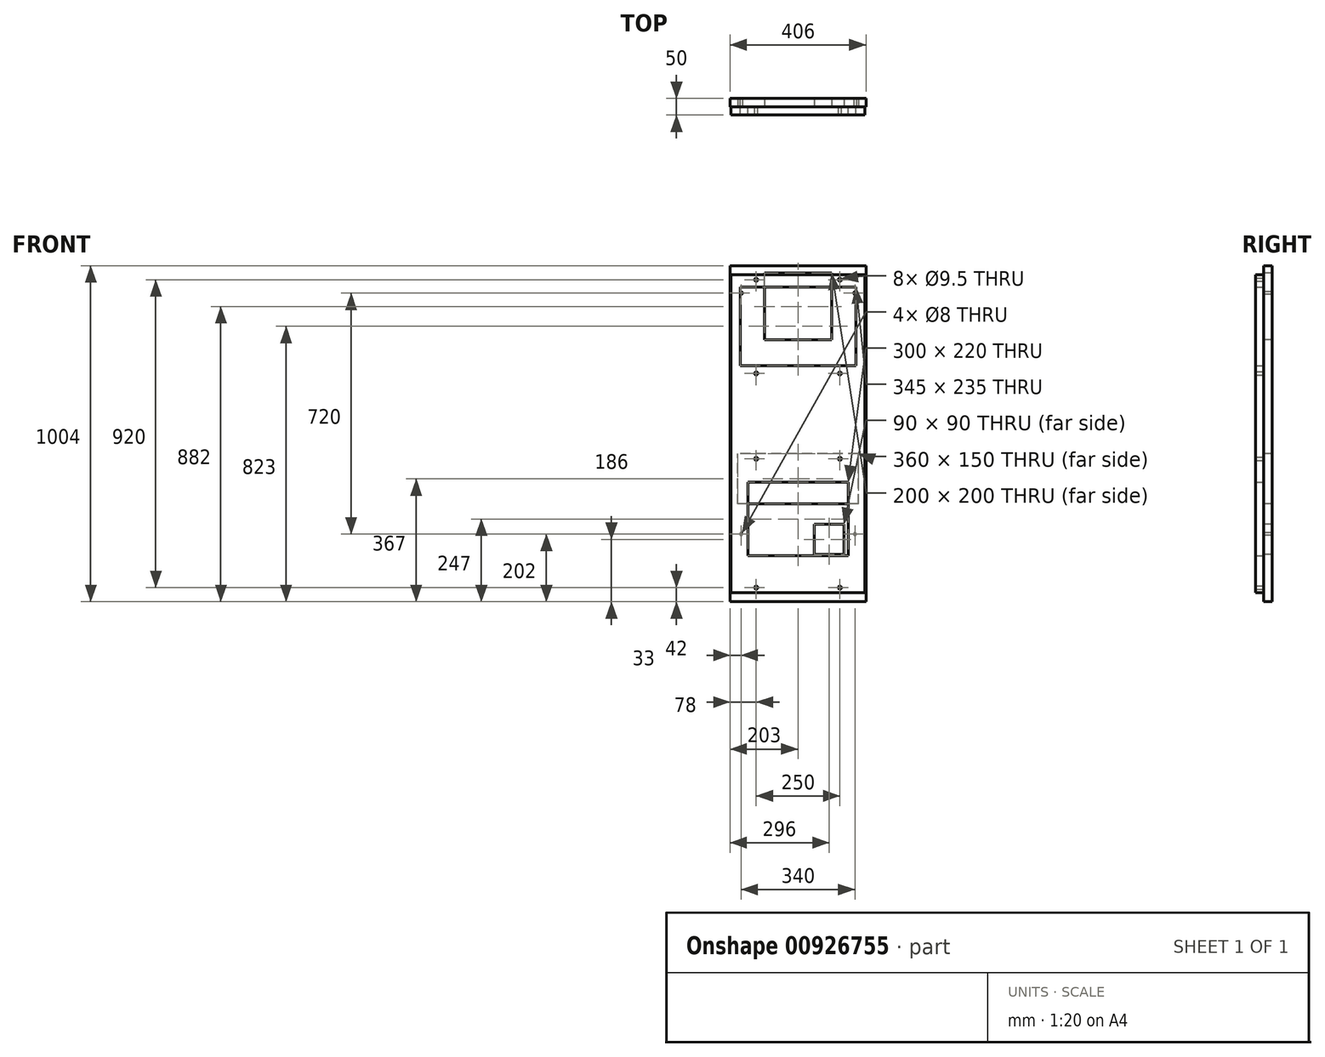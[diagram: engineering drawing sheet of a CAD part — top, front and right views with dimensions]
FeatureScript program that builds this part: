
annotation { "Feature Type Name" : "Feature", "Feature Type Description" : "" }
export const myFeature = defineFeature(function(context is Context, id is Id, definition is map)
    precondition{}
    {
        {
            var Q0;
            Q0=qCreatedBy(makeId("Front.planeOp"),FACE);
            var sketch = newSketch(context, id + "F0", { "sketchPlane" : qUnion([Q0])});
            skLineSegment(sketch, "E0.bottom", {"start": v(203, -502) * mm, "end": v(-203, -502) * mm});
            skLineSegment(sketch, "E0.top", {"start": v(203, 502) * mm, "end": v(-203, 502) * mm});
            skLineSegment(sketch, "E0.left", {"start": v(203, -502) * mm, "end": v(203, 502) * mm});
            skLineSegment(sketch, "E0.right", {"start": v(-203, -502) * mm, "end": v(-203, 502) * mm});
            skPoint(sketch, "E0.middle", {"position": v(0, 0) * mm});
            skLineSegment(sketch, "E1.bottom", {"start": v(100, 280) * mm, "end": v(-100, 280) * mm});
            skLineSegment(sketch, "E1.top", {"start": v(100, 480) * mm, "end": v(-100, 480) * mm});
            skLineSegment(sketch, "E1.left", {"start": v(100, 280) * mm, "end": v(100, 480) * mm});
            skLineSegment(sketch, "E1.right", {"start": v(-100, 280) * mm, "end": v(-100, 480) * mm});
            skPoint(sketch, "E1.middle", {"position": v(0, 380) * mm});
            skLineSegment(sketch, "E2.bottom", {"start": v(180, -210) * mm, "end": v(-180, -210) * mm});
            skLineSegment(sketch, "E2.top", {"start": v(180, -60) * mm, "end": v(-180, -60) * mm});
            skLineSegment(sketch, "E2.left", {"start": v(180, -210) * mm, "end": v(180, -60) * mm});
            skLineSegment(sketch, "E2.right", {"start": v(-180, -210) * mm, "end": v(-180, -60) * mm});
            skPoint(sketch, "E2.middle", {"position": v(0, -135) * mm});
            skLineSegment(sketch, "E3.bottom", {"start": v(48, -271) * mm, "end": v(138, -271) * mm});
            skLineSegment(sketch, "E3.top", {"start": v(48, -361) * mm, "end": v(138, -361) * mm});
            skLineSegment(sketch, "E3.left", {"start": v(48, -271) * mm, "end": v(48, -361) * mm});
            skLineSegment(sketch, "E3.right", {"start": v(138, -271) * mm, "end": v(138, -361) * mm});
            skCircle(sketch, "E4", {"center": v(170, 420) * mm, "radius": 4 * mm});
            skCircle(sketch, "E5", {"center": v(170, -300) * mm, "radius": 4 * mm});
            skCircle(sketch, "E6.MirrorC", {"center": v(-170, 420) * mm, "radius": 4 * mm});
            skCircle(sketch, "E7.MirrorC", {"center": v(-170, -300) * mm, "radius": 4 * mm});
            skSolve(sketch);
        }
        {
            var Q0;
            Q0 = qSketchRegion(id + "F0", true);
            extrude(context, id + "F1", {"entities" : qUnion([Q0]), "oppositeDirection" : true, "depth" : 25 * mm, "offsetDistance" : 25 * mm});
        }
        {
            var Q0;
            Q0=qCreatedBy(makeId("Front.planeOp"),FACE);
            var sketch = newSketch(context, id + "F2", { "sketchPlane" : qUnion([Q0])});
            skLineSegment(sketch, "E8.bottom", {"start": v(200, -475) * mm, "end": v(-200, -475) * mm});
            skLineSegment(sketch, "E8.top", {"start": v(200, 475) * mm, "end": v(-200, 475) * mm});
            skLineSegment(sketch, "E8.left", {"start": v(200, -475) * mm, "end": v(200, 475) * mm});
            skLineSegment(sketch, "E8.right", {"start": v(-200, -475) * mm, "end": v(-200, 475) * mm});
            skPoint(sketch, "E8.middle", {"position": v(0, 0) * mm});
            skLineSegment(sketch, "E9.bottom", {"start": v(172.5, 203.5) * mm, "end": v(-172.5, 203.5) * mm});
            skLineSegment(sketch, "E9.top", {"start": v(172.5, 438.5) * mm, "end": v(-172.5, 438.5) * mm});
            skLineSegment(sketch, "E9.left", {"start": v(172.5, 203.5) * mm, "end": v(172.5, 438.5) * mm});
            skLineSegment(sketch, "E9.right", {"start": v(-172.5, 203.5) * mm, "end": v(-172.5, 438.5) * mm});
            skPoint(sketch, "E9.middle", {"position": v(0, 321) * mm});
            skLineSegment(sketch, "E10.bottom", {"start": v(150, -365) * mm, "end": v(-150, -365) * mm});
            skLineSegment(sketch, "E10.top", {"start": v(150, -145) * mm, "end": v(-150, -145) * mm});
            skLineSegment(sketch, "E10.left", {"start": v(150, -365) * mm, "end": v(150, -145) * mm});
            skLineSegment(sketch, "E10.right", {"start": v(-150, -365) * mm, "end": v(-150, -145) * mm});
            skPoint(sketch, "E10.middle", {"position": v(0, -255) * mm});
            skCircle(sketch, "E11", {"center": v(125, 460) * mm, "radius": 4.75 * mm});
            skCircle(sketch, "E12", {"center": v(125, 180) * mm, "radius": 4.75 * mm});
            skCircle(sketch, "E13", {"center": v(125, -75) * mm, "radius": 4.75 * mm});
            skCircle(sketch, "E14", {"center": v(125, -460) * mm, "radius": 4.75 * mm});
            skCircle(sketch, "E15.MirrorC", {"center": v(-125, -460) * mm, "radius": 4.75 * mm});
            skCircle(sketch, "E16.MirrorC", {"center": v(-125, -75) * mm, "radius": 4.75 * mm});
            skCircle(sketch, "E17.MirrorC", {"center": v(-125, 180) * mm, "radius": 4.75 * mm});
            skCircle(sketch, "E18.MirrorC", {"center": v(-125, 460) * mm, "radius": 4.75 * mm});
            skSolve(sketch);
        }
        {
            var Q0;
            Q0 = qSketchRegion(id + "F2", true);
            extrude(context, id + "F3", {"entities" : qUnion([Q0]), "depth" : 25 * mm, "offsetDistance" : 25 * mm});
        }
    });
